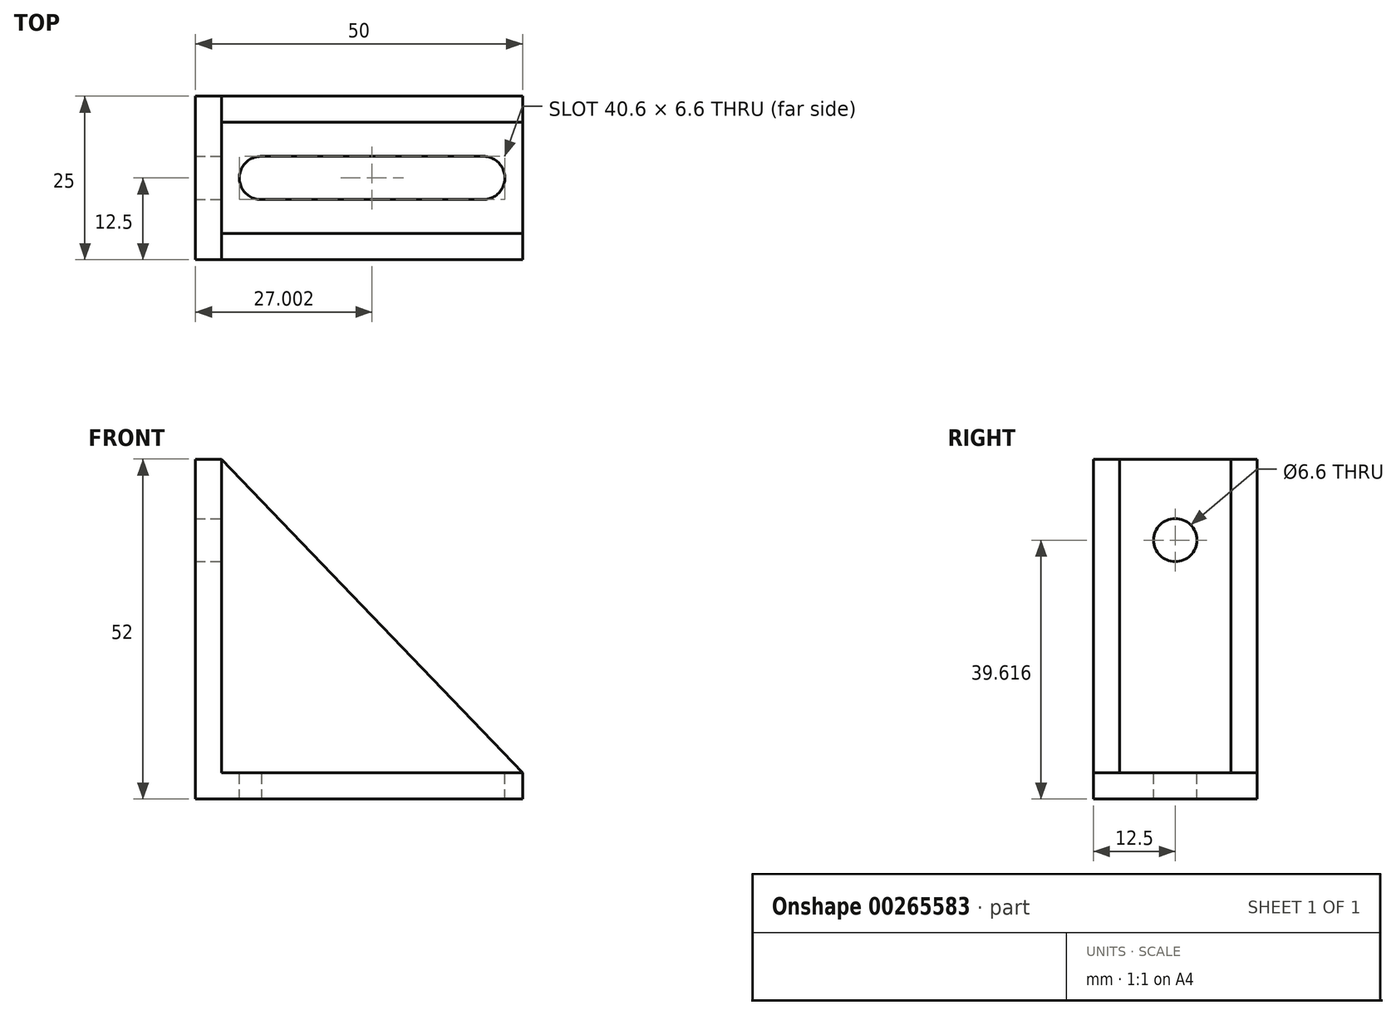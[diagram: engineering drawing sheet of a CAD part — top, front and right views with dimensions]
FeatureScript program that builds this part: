
annotation { "Feature Type Name" : "Feature", "Feature Type Description" : "" }
export const myFeature = defineFeature(function(context is Context, id is Id, definition is map)
    precondition{}
    {
        {
            var Q0;
            Q0=qCreatedBy(makeId("Front.planeOp"),FACE);
            var sketch = newSketch(context, id + "F0", { "sketchPlane" : qUnion([Q0])});
            skLineSegment(sketch, "E0", {"start": v(-19.44, 29.53) * mm, "end": v(-19.44, -22.47) * mm});
            skLineSegment(sketch, "E1", {"start": v(30.56, -22.47) * mm, "end": v(-19.44, -22.47) * mm});
            skLineSegment(sketch, "E2", {"start": v(30.56, -22.47) * mm, "end": v(30.56, -18.47) * mm});
            skLineSegment(sketch, "E3", {"start": v(30.56, -18.47) * mm, "end": v(-15.44, -18.47) * mm});
            skLineSegment(sketch, "E4", {"start": v(-15.44, -18.47) * mm, "end": v(-15.44, 29.53) * mm});
            skLineSegment(sketch, "E5", {"start": v(-15.44, 29.53) * mm, "end": v(-19.44, 29.53) * mm});
            skSolve(sketch);
        }
        {
            var Q0;
            Q0 = qSketchRegion(id + "F0", true);
            extrude(context, id + "F1", {"entities" : qUnion([Q0]), "depth" : 25 * mm});
        }
        {
            var Q0;
            Q0=makeQuery(id+"F1.opExtrude","CAP_FACE",FACE,{"disambiguationData":[OSD([sQuery(id+"F0.wireOp",EDGE,"E0"),sQuery(id+"F0.wireOp",EDGE,"E1"),sQuery(id+"F0.wireOp",EDGE,"E2"),sQuery(id+"F0.wireOp",EDGE,"E3"),sQuery(id+"F0.wireOp",EDGE,"E4"),sQuery(id+"F0.wireOp",EDGE,"E5")])],"isStart":false});
            var sketch = newSketch(context, id + "F2", { "sketchPlane" : qUnion([Q0])});
            skLineSegment(sketch, "E6", {"start": v(-15.44, 29.53) * mm, "end": v(30.56, -18.47) * mm});
            skLineSegment(sketch, "E7", {"start": v(30.56, -18.47) * mm, "end": v(-15.44, -18.47) * mm});
            skLineSegment(sketch, "E8", {"start": v(-15.44, -18.47) * mm, "end": v(-15.44, 29.53) * mm});
            skSolve(sketch);
        }
        {
            var Q0;
            Q0=makeQuery(id+"F2.imprint","IMPRINT",FACE,{"disambiguationData":[TD([[makeQuery(id+"F2.imprint","IMPRINT",EDGE,{"derivedFrom":sQuery(id+"F2.wireOp",EDGE,"E6")}),-1.0]])]});
            extrude(context, id + "F3", {"entities" : qUnion([Q0]), "oppositeDirection" : true, "depth" : 4 * mm});
        }
        {
            var Q0;
            Q0=makeQuery(id+"F1.opExtrude","CAP_FACE",FACE,{"disambiguationData":[OSD([sQuery(id+"F0.wireOp",EDGE,"E0"),sQuery(id+"F0.wireOp",EDGE,"E1"),sQuery(id+"F0.wireOp",EDGE,"E2"),sQuery(id+"F0.wireOp",EDGE,"E3"),sQuery(id+"F0.wireOp",EDGE,"E4"),sQuery(id+"F0.wireOp",EDGE,"E5")])],"isStart":true});
            var sketch = newSketch(context, id + "F4", { "sketchPlane" : qUnion([Q0])});
            skLineSegment(sketch, "E9", {"start": v(15.44, 29.53) * mm, "end": v(-30.56, -18.47) * mm});
            skLineSegment(sketch, "E10", {"start": v(-30.56, -18.47) * mm, "end": v(15.44, -18.47) * mm});
            skLineSegment(sketch, "E11", {"start": v(15.44, -18.47) * mm, "end": v(15.44, 29.53) * mm});
            skSolve(sketch);
        }
        {
            var Q0;
            Q0=makeQuery(id+"F4.imprint","IMPRINT",FACE,{"disambiguationData":[TD([[makeQuery(id+"F4.imprint","IMPRINT",EDGE,{"derivedFrom":sQuery(id+"F4.wireOp",EDGE,"E9")}),1.0]])]});
            extrude(context, id + "F5", {"entities" : qUnion([Q0]), "oppositeDirection" : true, "depth" : 4 * mm});
        }
        {
            var Q0;
            Q0=makeQuery(id+"F1.opExtrude","SWEPT_FACE",FACE,{"disambiguationData":[OSD([sQuery(id+"F0.wireOp",EDGE,"E4")])]});
            var sketch = newSketch(context, id + "F6", { "sketchPlane" : qUnion([Q0])});
            skPoint(sketch, "E12", {"position": v(-12.5, 17.15) * mm});
            skPoint(sketch, "E12.positionSnap0", {"position": v(-12.5, 29.53) * mm});
            skSolve(sketch);
        }
        {
            var Q0;
            Q0=sQuery(id+"F6.wireOp",VERTEX,"E12");
            var Q1;
            Q1=makeQuery(id+"F1.opExtrude","SWEPT_BODY",BODY,{"disambiguationData":[OSD([sQuery(id+"F0.wireOp",EDGE,"E0"),sQuery(id+"F0.wireOp",EDGE,"E1"),sQuery(id+"F0.wireOp",EDGE,"E2"),sQuery(id+"F0.wireOp",EDGE,"E3"),sQuery(id+"F0.wireOp",EDGE,"E4"),sQuery(id+"F0.wireOp",EDGE,"E5")])]});
            hole(context, id + "F7", {"style" : HoleStyle.SIMPLE, "endStyle" : HoleEndStyle.THROUGH, "standardTappedOrClearance" : lookupTablePath({ "standard" : "ISO", "fit" : "Normal", "size" : "M6", "type" : "Clearance" }), "standardBlindInLast" : lookupTablePath({ "fit" : "Standard", "standard" : "ISO", "size" : "M6", "type" : "Clearance" }), "holeDiameter" : 6.6 * mm, "tappedDepth" : 12 * mm, "tapClearance" : 3, "locations" : qUnion([Q0]), "scope" : qUnion([Q1])});
        }
        {
            var Q0;
            Q0=makeQuery(id+"F1.opExtrude","SWEPT_FACE",FACE,{"disambiguationData":[OSD([sQuery(id+"F0.wireOp",EDGE,"E3")])]});
            var sketch = newSketch(context, id + "F8", { "sketchPlane" : qUnion([Q0])});
            skPoint(sketch, "E13", {"position": v(-9.44, -12.5) * mm});
            skPoint(sketch, "E13.positionSnap0", {"position": v(-15.44, -12.5) * mm});
            skPoint(sketch, "E14", {"position": v(24.56, -12.5) * mm});
            skPoint(sketch, "E14.positionSnap0", {"position": v(30.56, -12.5) * mm});
            skSolve(sketch);
        }
        {
            var Q0;
            Q0=sQuery(id+"F8.wireOp",VERTEX,"E13");
            var Q1;
            Q1=sQuery(id+"F8.wireOp",VERTEX,"E14");
            var Q2;
            Q2=makeQuery(id+"F1.opExtrude","SWEPT_BODY",BODY,{"disambiguationData":[OSD([sQuery(id+"F0.wireOp",EDGE,"E0"),sQuery(id+"F0.wireOp",EDGE,"E1"),sQuery(id+"F0.wireOp",EDGE,"E2"),sQuery(id+"F0.wireOp",EDGE,"E3"),sQuery(id+"F0.wireOp",EDGE,"E4"),sQuery(id+"F0.wireOp",EDGE,"E5")])]});
            hole(context, id + "F9", {"style" : HoleStyle.SIMPLE, "endStyle" : HoleEndStyle.THROUGH, "standardTappedOrClearance" : lookupTablePath({ "standard" : "ISO", "fit" : "Normal", "size" : "M6", "type" : "Clearance" }), "standardBlindInLast" : lookupTablePath({ "fit" : "Standard", "standard" : "ISO", "size" : "M6", "type" : "Clearance" }), "holeDiameter" : 6.6 * mm, "tappedDepth" : 12 * mm, "tapClearance" : 3, "locations" : qUnion([Q0, Q1]), "scope" : qUnion([Q2])});
        }
        {
            var Q0;
            Q0=makeQuery(id+"F1.opExtrude","SWEPT_FACE",FACE,{"disambiguationData":[OSD([sQuery(id+"F0.wireOp",EDGE,"E3")])]});
            var sketch = newSketch(context, id + "F10", { "sketchPlane" : qUnion([Q0])});
            skLineSegment(sketch, "E15", {"start": v(-9.27, -15.8) * mm, "end": v(24.56, -15.8) * mm});
            skLineSegment(sketch, "E16", {"start": v(24.56, -15.8) * mm, "end": v(24.56, -9.2) * mm});
            skLineSegment(sketch, "E17", {"start": v(24.56, -9.2) * mm, "end": v(-9.6, -9.2) * mm});
            skLineSegment(sketch, "E18", {"start": v(-9.6, -9.2) * mm, "end": v(-9.27, -15.8) * mm});
            skSolve(sketch);
        }
        {
            var Q0;
            {var subQ0=sQuery(id+"F10.wireOp",EDGE,"E15");Q0=makeQuery(id+"F10.imprint","IMPRINT",FACE,{"disambiguationData":[TD([[makeQuery(id+"F10.imprint","IMPRINT",EDGE,{"derivedFrom":subQ0}),1.0]])]});}
            extrude(context, id + "F11", {"entities" : qUnion([Q0]), "operationType" : NewBodyOperationType.REMOVE, "oppositeDirection" : true, "depth" : 25 * mm});
        }
    });
